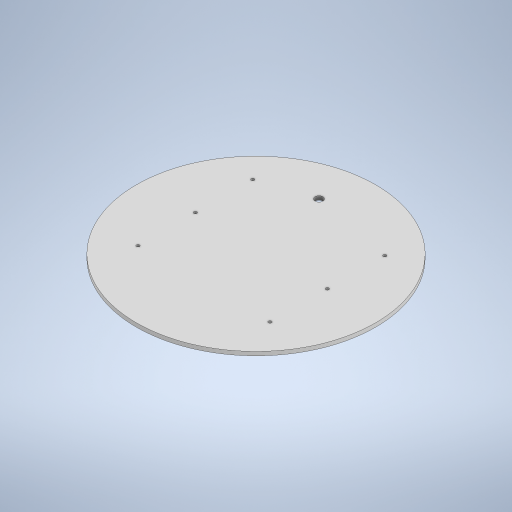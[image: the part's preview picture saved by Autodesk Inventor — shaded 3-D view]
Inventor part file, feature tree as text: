
AUTODESK INVENTOR PART (.ipt)
format: ipt  version: 2023 (Build 270158000, 158)  size: 248,320 bytes
history: native  units: mm
features: sketch x3, extrude x2, other x1, hole x1
ambient origin geometry x8: Origin, YZ Plane, XZ Plane, XY Plane, X Axis, Y Axis, Z Axis, Center Point
bodies: Body1 (feature_tree)
feature tree (7):
  other  "ソリッド1"
  extrude  "押し出し1"  Depth=250.0mm
  extrude  "押し出し2"  Depth=4.0mm TaperAngle=0.0deg
  hole  "穴1"  [1 undecoded]
  sketch  "スケッチ1"
  sketch  "スケッチ2"
  sketch  "スケッチ4"
note: 1 required parameter value undecoded (feature->parameter linkage not recoverable at this tier; creation-order binding heuristic only, values carry confidence <= 0.55)
